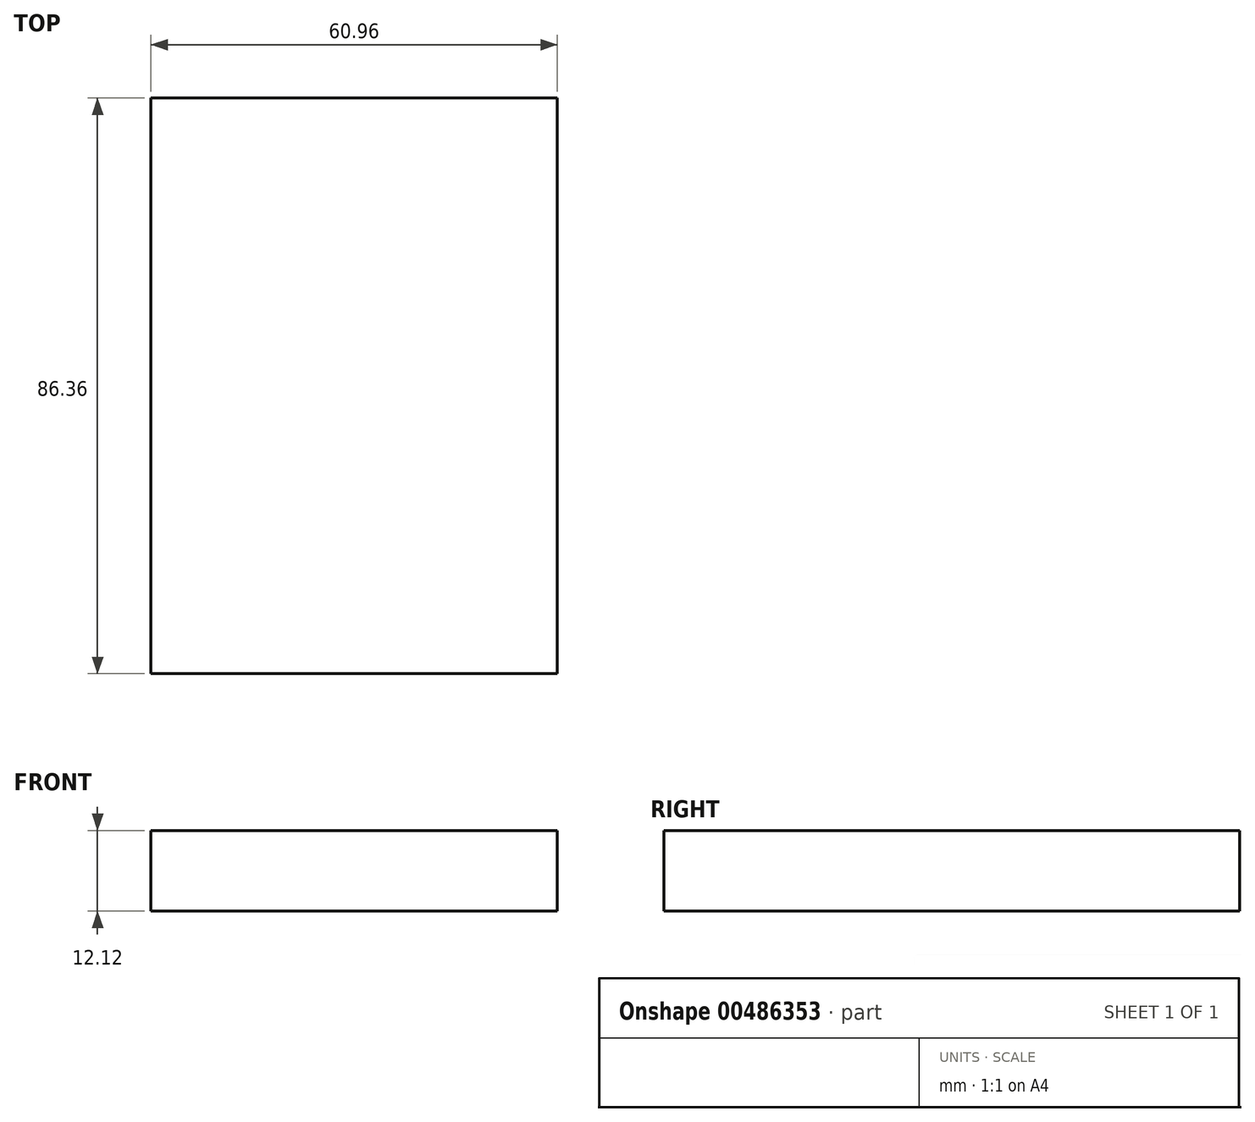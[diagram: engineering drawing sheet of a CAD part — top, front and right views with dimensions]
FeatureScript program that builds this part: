
annotation { "Feature Type Name" : "Feature", "Feature Type Description" : "" }
export const myFeature = defineFeature(function(context is Context, id is Id, definition is map)
    precondition{}
    {
        {
            var Q0;
            Q0=qCreatedBy(makeId("Top.planeOp"),FACE);
            var sketch = newSketch(context, id + "F0", { "sketchPlane" : qUnion([Q0])});
            skLineSegment(sketch, "E0.bottom", {"start": v(-38.34, 40.5) * mm, "end": v(22.62, 40.5) * mm});
            skLineSegment(sketch, "E0.top", {"start": v(-38.34, -45.86) * mm, "end": v(22.62, -45.86) * mm});
            skLineSegment(sketch, "E0.left", {"start": v(-38.34, 40.5) * mm, "end": v(-38.34, -45.86) * mm});
            skLineSegment(sketch, "E0.right", {"start": v(22.62, 40.5) * mm, "end": v(22.62, -45.86) * mm});
            skSolve(sketch);
        }
        {
            var Q0;
            Q0=makeQuery(id+"F0.imprint","IMPRINT",FACE,{"disambiguationData":[TD([[makeQuery(id+"F0.imprint","IMPRINT",EDGE,{"derivedFrom":sQuery(id+"F0.wireOp",EDGE,"E0.bottom")}),-1.0]])]});
            extrude(context, id + "F1", {"entities" : qUnion([Q0]), "depth" : 12.12 * mm, "offsetDistance" : 25.4 * mm});
        }
    });
